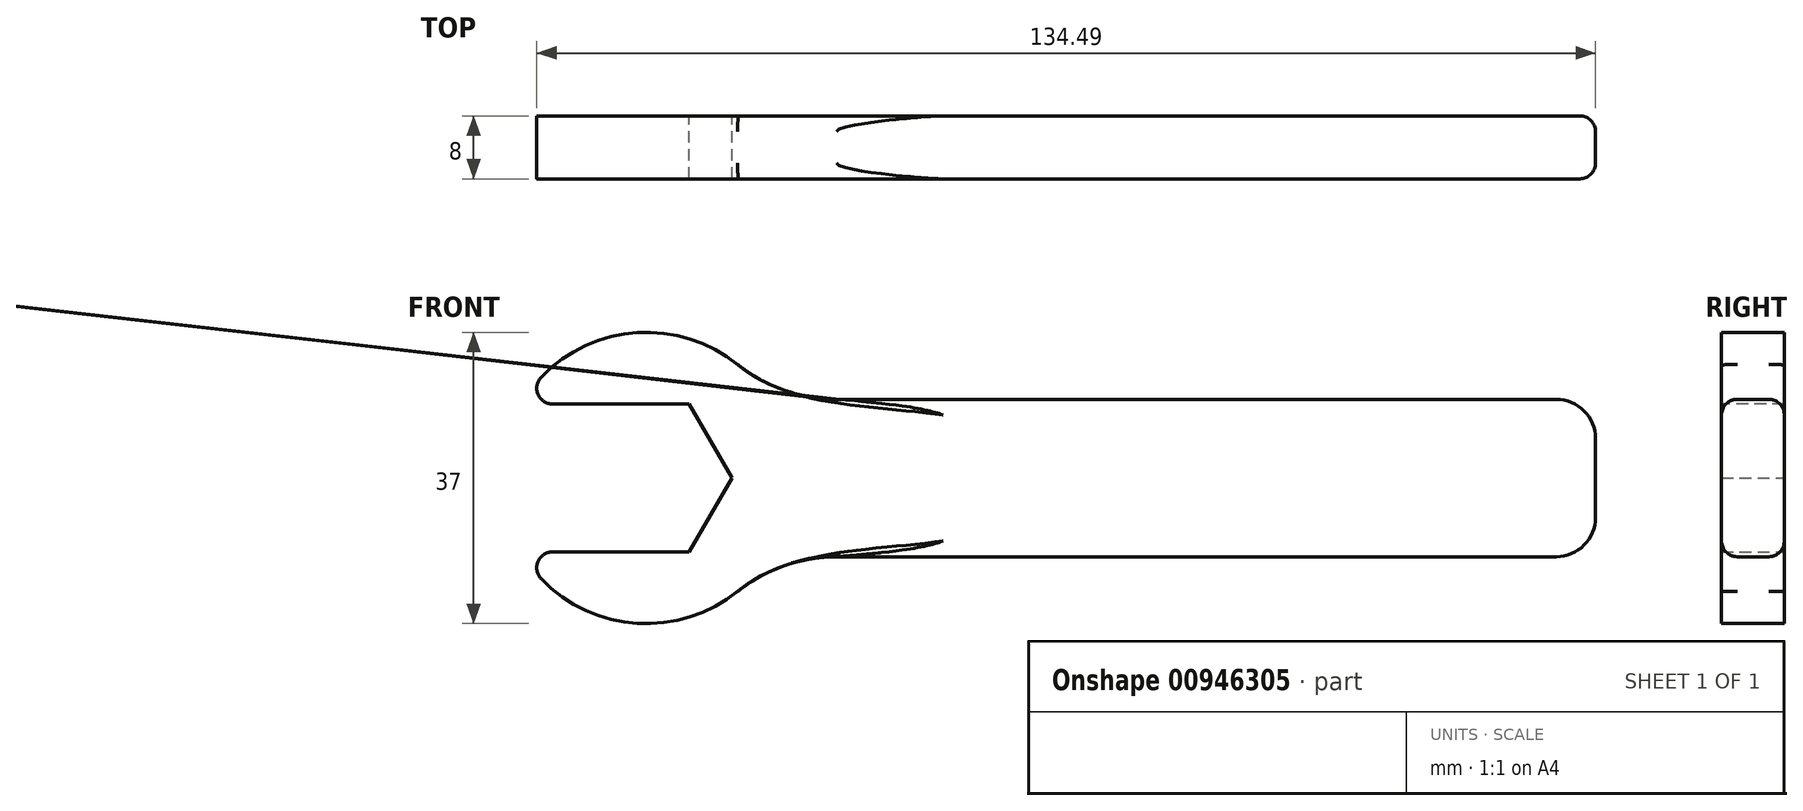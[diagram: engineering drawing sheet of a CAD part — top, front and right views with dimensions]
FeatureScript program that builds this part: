
annotation { "Feature Type Name" : "Feature", "Feature Type Description" : "" }
export const myFeature = defineFeature(function(context is Context, id is Id, definition is map)
    precondition{}
    {
        {
            var Q0;
            Q0=qCreatedBy(makeId("Front.planeOp"),FACE);
            var sketch = newSketch(context, id + "F0", { "sketchPlane" : qUnion([Q0])});
            skArc(sketch, "E0", {"start": v(-15.93, -9.4) * mm, "mid": v(18.5, 0) * mm, "end": v(-15.93, 9.4) * mm});
            skCircle(sketch, "E1.cCircle", {"center": v(0, 0) * mm, "radius": 9.4 * mm, "construction": true});
            skLineSegment(sketch, "E1.0", {"start": v(-5.43, 9.4) * mm, "end": v(5.43, 9.4) * mm});
            skLineSegment(sketch, "E1.1", {"start": v(5.43, 9.4) * mm, "end": v(10.85, 0) * mm});
            skLineSegment(sketch, "E1.2", {"start": v(10.85, 0) * mm, "end": v(5.43, -9.4) * mm});
            skLineSegment(sketch, "E1.3", {"start": v(5.43, -9.4) * mm, "end": v(1.83, -9.4) * mm});
            skPoint(sketch, "E1.0.midPoint", {"position": v(0, 9.4) * mm});
            skLineSegment(sketch, "E2.bottom", {"start": v(15.56, 10) * mm, "end": v(120.56, 10) * mm});
            skLineSegment(sketch, "E2.top", {"start": v(15.56, -10) * mm, "end": v(120.56, -10) * mm});
            skLineSegment(sketch, "E2.left", {"start": v(15.56, 10) * mm, "end": v(15.56, -10) * mm});
            skLineSegment(sketch, "E2.right", {"start": v(120.56, 10) * mm, "end": v(120.56, -10) * mm});
            skLineSegment(sketch, "E3", {"start": v(-5.43, 9.4) * mm, "end": v(-15.93, 9.4) * mm});
            skLineSegment(sketch, "E4", {"start": v(1.83, -9.4) * mm, "end": v(-15.93, -9.4) * mm});
            skSolve(sketch);
        }
        {
            var Q0;
            Q0=makeQuery(id+"F0.imprint","IMPRINT",FACE,{"disambiguationData":[TD([[makeQuery(id+"F0.imprint","IMPRINT",EDGE,{"derivedFrom":sQuery(id+"F0.wireOp",EDGE,"E1.0")}),1.0]])]});
            var Q1;
            {var subQ0=sQuery(id+"F0.wireOp",EDGE,"E2.left");Q1=makeQuery(id+"F0.imprint","IMPRINT",FACE,{"disambiguationData":[TD([[makeQuery(id+"F0.imprint","IMPRINT",EDGE,{"derivedFrom":subQ0}),1.0]])]});}
            var Q2;
            {var subQ1=sQuery(id+"F0.wireOp",EDGE,"E2.bottom");Q2=makeQuery(id+"F0.imprint","IMPRINT",FACE,{"disambiguationData":[TD([[makeQuery(id+"F0.imprint","IMPRINT",EDGE,{"derivedFrom":subQ1}),-1.0]])]});}
            extrude(context, id + "F1", {"entities" : qUnion([Q0, Q1, Q2]), "depth" : 8 * mm, "offsetDistance" : 25 * mm});
        }
        {
            var Q0;
            Q0=makeQuery(id+"F1.opExtrude","SWEPT_EDGE",EDGE,{"disambiguationData":[OSD([sQuery(id+"F0.wireOp",EDGE,"E0"),sQuery(id+"F0.wireOp",EDGE,"E3")])]});
            var Q1;
            Q1=makeQuery(id+"F1.opExtrude","SWEPT_EDGE",EDGE,{"disambiguationData":[OSD([sQuery(id+"F0.wireOp",EDGE,"E0"),sQuery(id+"F0.wireOp",EDGE,"E4")])]});
            fillet(context, id + "F2", {"entities" : qUnion([Q0, Q1]), "radius" : 2 * mm, "tangentPropagation" : true, "allowEdgeOverflow" : false});
        }
        {
            var Q0;
            Q0=makeQuery(id+"F1.opExtrude","SWEPT_EDGE",EDGE,{"disambiguationData":[OSD([sQuery(id+"F0.wireOp",EDGE,"E2.bottom"),sQuery(id+"F0.wireOp",EDGE,"E2.right")])]});
            var Q1;
            Q1=makeQuery(id+"F1.opExtrude","SWEPT_EDGE",EDGE,{"disambiguationData":[OSD([sQuery(id+"F0.wireOp",EDGE,"E2.top"),sQuery(id+"F0.wireOp",EDGE,"E2.right")])]});
            fillet(context, id + "F3", {"entities" : qUnion([Q0, Q1]), "radius" : 5 * mm, "tangentPropagation" : true, "allowEdgeOverflow" : false});
        }
        {
            var Q0;
            Q0=makeQuery(id+"F1.opExtrude","CAP_EDGE",EDGE,{"disambiguationData":[OSD([sQuery(id+"F0.wireOp",EDGE,"E2.bottom")])],"isStart":true});
            var Q1;
            Q1=makeQuery(id+"F1.opExtrude","CAP_EDGE",EDGE,{"disambiguationData":[OSD([sQuery(id+"F0.wireOp",EDGE,"E2.bottom")])],"isStart":false});
            fillet(context, id + "F4", {"entities" : qUnion([Q0, Q1]), "radius" : 2 * mm, "tangentPropagation" : true, "allowEdgeOverflow" : false});
        }
        {
            var Q0;
            Q0=makeQuery(id+"F1.opExtrude","SWEPT_EDGE",EDGE,{"disambiguationData":[OSD([sQuery(id+"F0.wireOp",EDGE,"E0"),sQuery(id+"F0.wireOp",EDGE,"E2.top"),sQuery(id+"F0.wireOp",EDGE,"E2.left")])]});
            var Q1;
            Q1=makeQuery(id+"F1.opExtrude","SWEPT_EDGE",EDGE,{"disambiguationData":[OSD([sQuery(id+"F0.wireOp",EDGE,"E0"),sQuery(id+"F0.wireOp",EDGE,"E2.bottom"),sQuery(id+"F0.wireOp",EDGE,"E2.left")])]});
            fillet(context, id + "F5", {"entities" : qUnion([Q0, Q1]), "radius" : 20 * mm, "tangentPropagation" : true, "defaultsChanged" : true, "vertexSettings" : [], "allowEdgeOverflow" : false});
        }
    });
